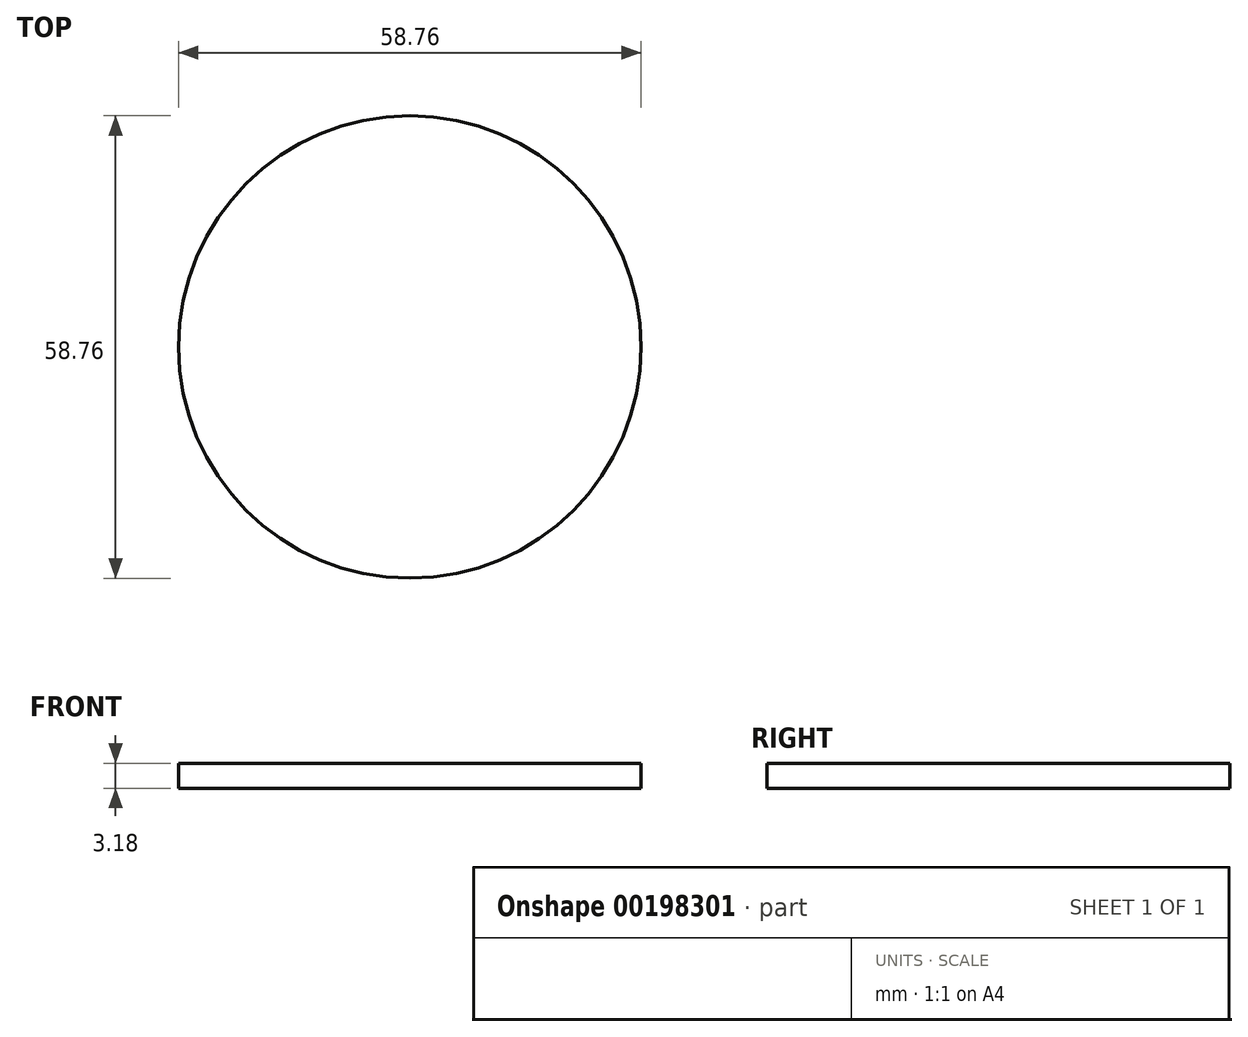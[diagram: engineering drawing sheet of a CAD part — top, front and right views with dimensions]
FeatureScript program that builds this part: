
annotation { "Feature Type Name" : "Feature", "Feature Type Description" : "" }
export const myFeature = defineFeature(function(context is Context, id is Id, definition is map)
    precondition{}
    {
        {
            var Q0;
            Q0=qCreatedBy(makeId("Top.planeOp"),FACE);
            var sketch = newSketch(context, id + "F0", { "sketchPlane" : qUnion([Q0])});
            skCircle(sketch, "E0", {"center": v(0, 0) * mm, "radius": 29.38 * mm});
            skSolve(sketch);
        }
        {
            var Q0;
            Q0=makeQuery(id+"F0.imprint","IMPRINT",FACE,{"disambiguationData":[TD([[makeQuery(id+"F0.imprint","IMPRINT",EDGE,{"derivedFrom":sQuery(id+"F0.wireOp",EDGE,"E0")}),1.0]])]});
            extrude(context, id + "F1", {"entities" : qUnion([Q0]), "endBound" : BoundingType.SYMMETRIC, "depth" : 3.17 * mm});
        }
    });
